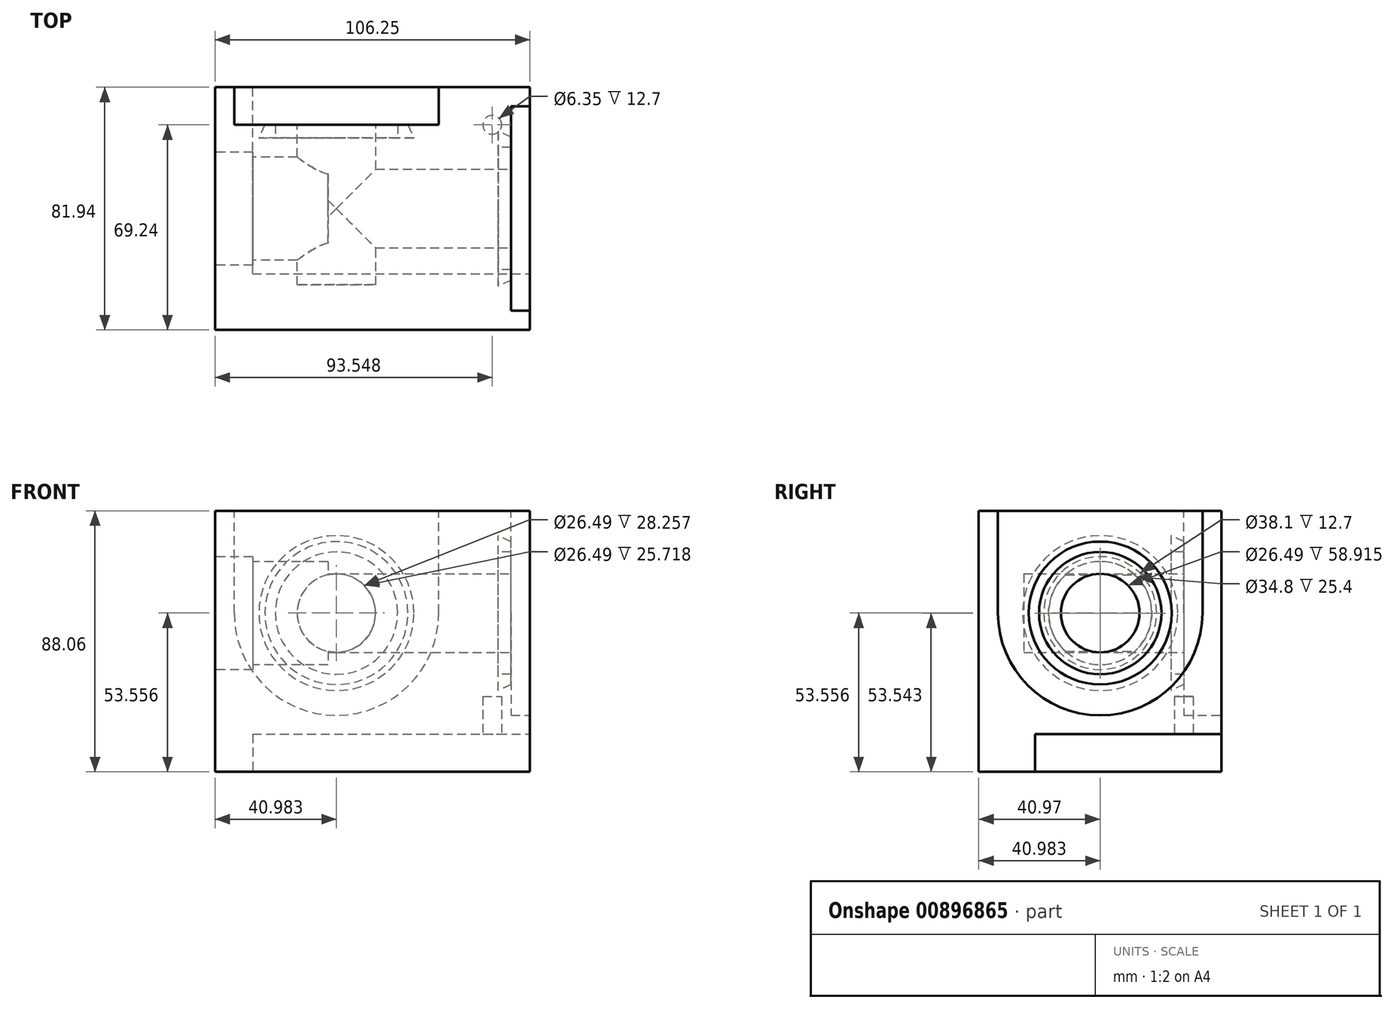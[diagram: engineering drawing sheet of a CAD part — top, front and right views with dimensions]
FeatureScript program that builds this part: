
annotation { "Feature Type Name" : "Feature", "Feature Type Description" : "" }
export const myFeature = defineFeature(function(context is Context, id is Id, definition is map)
    precondition{}
    {
        {
            var Q0;
            Q0=qCreatedBy(makeId("Top.planeOp"),FACE);
            var sketch = newSketch(context, id + "F0", { "sketchPlane" : qUnion([Q0])});
            skLineSegment(sketch, "E0.bottom", {"start": v(0, 0) * mm, "end": v(106.25, 0) * mm});
            skLineSegment(sketch, "E0.top", {"start": v(0, 81.94) * mm, "end": v(106.25, 81.94) * mm});
            skLineSegment(sketch, "E0.left", {"start": v(0, 0) * mm, "end": v(0, 81.94) * mm});
            skLineSegment(sketch, "E0.right", {"start": v(106.25, 0) * mm, "end": v(106.25, 81.94) * mm});
            skSolve(sketch);
        }
        {
            var Q0;
            Q0 = qSketchRegion(id + "F0", true);
            extrude(context, id + "F1", {"entities" : qUnion([Q0]), "depth" : 88.06 * mm, "offsetDistance" : 25.4 * mm});
        }
        {
            var Q0;
            Q0=makeQuery(id+"F1.opExtrude","SWEPT_FACE",FACE,{"disambiguationData":[OSD([sQuery(id+"F0.wireOp",EDGE,"E0.right")])]});
            var sketch = newSketch(context, id + "F2", { "sketchPlane" : qUnion([Q0])});
            skLineSegment(sketch, "E1.bottom", {"start": v(19.02, 0) * mm, "end": v(81.94, 0) * mm});
            skLineSegment(sketch, "E1.top", {"start": v(19.02, 12.7) * mm, "end": v(81.94, 12.7) * mm});
            skLineSegment(sketch, "E1.left", {"start": v(19.02, 0) * mm, "end": v(19.02, 12.7) * mm});
            skLineSegment(sketch, "E1.right", {"start": v(81.94, 0) * mm, "end": v(81.94, 12.7) * mm});
            skSolve(sketch);
        }
        {
            var Q0;
            Q0 = qSketchRegion(id + "F2", true);
            extrude(context, id + "F3", {"entities" : qUnion([Q0]), "operationType" : NewBodyOperationType.REMOVE, "oppositeDirection" : true, "depth" : 93.55 * mm, "offsetDistance" : 25.4 * mm});
        }
        {
            var Q0;
            Q0=makeQuery(id+"F1.opExtrude","SWEPT_FACE",FACE,{"disambiguationData":[OSD([sQuery(id+"F0.wireOp",EDGE,"E0.right")])]});
            var sketch = newSketch(context, id + "F4", { "sketchPlane" : qUnion([Q0])});
            skLineSegment(sketch, "E2.bottom", {"start": v(6.48, 53.56) * mm, "end": v(75.49, 53.56) * mm});
            skLineSegment(sketch, "E2.top", {"start": v(6.48, 88.06) * mm, "end": v(75.49, 88.06) * mm});
            skLineSegment(sketch, "E2.left", {"start": v(6.48, 53.56) * mm, "end": v(6.48, 88.06) * mm});
            skLineSegment(sketch, "E2.right", {"start": v(75.49, 53.56) * mm, "end": v(75.49, 88.06) * mm});
            skArc(sketch, "E3", {"start": v(75.49, 53.56) * mm, "mid": v(40.98, 19.05) * mm, "end": v(6.48, 53.56) * mm});
            skSolve(sketch);
        }
        {
            var Q0;
            Q0 = qSketchRegion(id + "F4", true);
            extrude(context, id + "F5", {"entities" : qUnion([Q0]), "operationType" : NewBodyOperationType.REMOVE, "oppositeDirection" : true, "depth" : 6.35 * mm, "offsetDistance" : 25.4 * mm});
        }
        {
            var Q0;
            Q0=makeQuery(id+"F1.opExtrude","SWEPT_FACE",FACE,{"disambiguationData":[OSD([sQuery(id+"F0.wireOp",EDGE,"E0.top")])]});
            var sketch = newSketch(context, id + "F6", { "sketchPlane" : qUnion([Q0])});
            skLineSegment(sketch, "E4.bottom", {"start": v(-75.49, 53.56) * mm, "end": v(-6.48, 53.56) * mm});
            skLineSegment(sketch, "E4.top", {"start": v(-75.49, 88.06) * mm, "end": v(-6.48, 88.06) * mm});
            skLineSegment(sketch, "E4.left", {"start": v(-75.49, 53.56) * mm, "end": v(-75.49, 88.06) * mm});
            skLineSegment(sketch, "E4.right", {"start": v(-6.48, 53.56) * mm, "end": v(-6.48, 88.06) * mm});
            skArc(sketch, "E5", {"start": v(-6.48, 53.56) * mm, "mid": v(-40.98, 19.05) * mm, "end": v(-75.49, 53.56) * mm});
            skSolve(sketch);
        }
        {
            var Q0;
            Q0 = qSketchRegion(id + "F6", true);
            extrude(context, id + "F7", {"entities" : qUnion([Q0]), "operationType" : NewBodyOperationType.REMOVE, "oppositeDirection" : true, "depth" : 12.7 * mm, "offsetDistance" : 25.4 * mm});
        }
        {
            var Q0;
            Q0=makeQuery(id+"F5.boolean.opBoolean","COPY",FACE,{"derivedFrom":makeQuery(id+"F5.opExtrude","CAP_FACE",FACE,{"disambiguationData":[OSD([sQuery(id+"F4.wireOp",EDGE,"E2.top"),sQuery(id+"F4.wireOp",EDGE,"E2.left"),sQuery(id+"F4.wireOp",EDGE,"E2.right"),sQuery(id+"F4.wireOp",EDGE,"E3")])],"isStart":false})});
            var sketch = newSketch(context, id + "F8", { "sketchPlane" : qUnion([Q0])});
            skCircle(sketch, "E6", {"center": v(40.98, 53.56) * mm, "radius": 13.25 * mm});
            skSolve(sketch);
        }
        {
            var Q0;
            Q0 = qSketchRegion(id + "F8", true);
            extrude(context, id + "F9", {"entities" : qUnion([Q0]), "operationType" : NewBodyOperationType.REMOVE, "oppositeDirection" : true, "depth" : 69.01 * mm, "offsetDistance" : 25.4 * mm});
        }
        {
            var Q0;
            Q0=makeQuery(id+"F7.boolean.opBoolean","COPY",FACE,{"derivedFrom":makeQuery(id+"F7.opExtrude","CAP_FACE",FACE,{"disambiguationData":[OSD([sQuery(id+"F6.wireOp",EDGE,"E4.top"),sQuery(id+"F6.wireOp",EDGE,"E4.left"),sQuery(id+"F6.wireOp",EDGE,"E4.right"),sQuery(id+"F6.wireOp",EDGE,"E5")])],"isStart":false})});
            var sketch = newSketch(context, id + "F10", { "sketchPlane" : qUnion([Q0])});
            skCircle(sketch, "E7", {"center": v(-40.98, 53.56) * mm, "radius": 13.25 * mm});
            skSolve(sketch);
        }
        {
            var Q0;
            Q0 = qSketchRegion(id + "F10", true);
            extrude(context, id + "F11", {"entities" : qUnion([Q0]), "operationType" : NewBodyOperationType.REMOVE, "oppositeDirection" : true, "depth" : 53.97 * mm, "offsetDistance" : 25.4 * mm});
        }
        {
            var Q0;
            Q0=makeQuery(id+"F1.opExtrude","SWEPT_FACE",FACE,{"disambiguationData":[OSD([sQuery(id+"F0.wireOp",EDGE,"E0.left")])]});
            var sketch = newSketch(context, id + "F12", { "sketchPlane" : qUnion([Q0])});
            skCircle(sketch, "E8", {"center": v(-40.97, 53.54) * mm, "radius": 19.05 * mm});
            skSolve(sketch);
        }
        {
            var Q0;
            Q0 = qSketchRegion(id + "F12", true);
            extrude(context, id + "F13", {"entities" : qUnion([Q0]), "operationType" : NewBodyOperationType.REMOVE, "oppositeDirection" : true, "depth" : 12.7 * mm, "offsetDistance" : 25.4 * mm});
        }
        {
            var Q0;
            Q0=makeQuery(id+"F3.boolean.opBoolean","COPY",FACE,{"derivedFrom":makeQuery(id+"F3.opExtrude","SWEPT_FACE",FACE,{"disambiguationData":[OSD([sQuery(id+"F2.wireOp",EDGE,"E1.top")])]})});
            var sketch = newSketch(context, id + "F14", { "sketchPlane" : qUnion([Q0])});
            skCircle(sketch, "E9", {"center": v(93.55, -69.24) * mm, "radius": 3.18 * mm});
            skSolve(sketch);
        }
        {
            var Q0;
            Q0 = qSketchRegion(id + "F14", true);
            extrude(context, id + "F15", {"entities" : qUnion([Q0]), "operationType" : NewBodyOperationType.REMOVE, "oppositeDirection" : true, "depth" : 12.7 * mm, "offsetDistance" : 25.4 * mm});
        }
        {
            var Q0;
            Q0=makeQuery(id+"F5.boolean.opBoolean","COPY",FACE,{"derivedFrom":makeQuery(id+"F5.opExtrude","CAP_FACE",FACE,{"disambiguationData":[OSD([sQuery(id+"F4.wireOp",EDGE,"E2.top"),sQuery(id+"F4.wireOp",EDGE,"E2.left"),sQuery(id+"F4.wireOp",EDGE,"E2.right"),sQuery(id+"F4.wireOp",EDGE,"E3")])],"isStart":false})});
            var sketch = newSketch(context, id + "F16", { "sketchPlane" : qUnion([Q0])});
            skCircle(sketch, "E10", {"center": v(40.98, 53.56) * mm, "radius": 24.12 * mm});
            skSolve(sketch);
        }
        {
            var Q0;
            Q0 = qSketchRegion(id + "F16", true);
            extrude(context, id + "F17", {"entities" : qUnion([Q0]), "operationType" : NewBodyOperationType.REMOVE, "oppositeDirection" : true, "depth" : 4.37 * mm, "offsetDistance" : 25.4 * mm, "hasDraft" : true, "draftAngle" : 25 * degree});
        }
        {
            var Q0;
            Q0=makeQuery(id+"F17.boolean.opBoolean","COPY",FACE,{"derivedFrom":makeQuery(id+"F17.opExtrude","CAP_FACE",FACE,{"disambiguationData":[OSD([sQuery(id+"F16.wireOp",EDGE,"E10")])],"isStart":false})});
            var sketch = newSketch(context, id + "F18", { "sketchPlane" : qUnion([Q0])});
            skCircle(sketch, "E11", {"center": v(40.98, 53.56) * mm, "radius": 20.64 * mm});
            skSolve(sketch);
        }
        {
            var Q0;
            Q0 = qSketchRegion(id + "F18", true);
            extrude(context, id + "F19", {"entities" : qUnion([Q0]), "operationType" : NewBodyOperationType.ADD, "depth" : 4.37 * mm, "offsetDistance" : 25.4 * mm});
        }
        {
            var Q0;
            Q0=makeQuery(id+"F19.opExtrude","CAP_FACE",FACE,{"disambiguationData":[OSD([sQuery(id+"F18.wireOp",EDGE,"E11")])],"isStart":false});
            var sketch = newSketch(context, id + "F20", { "sketchPlane" : qUnion([Q0])});
            skCircle(sketch, "E12", {"center": v(40.98, 53.56) * mm, "radius": 13.25 * mm});
            skSolve(sketch);
        }
        {
            var Q0;
            Q0 = qSketchRegion(id + "F20", true);
            extrude(context, id + "F21", {"entities" : qUnion([Q0]), "operationType" : NewBodyOperationType.REMOVE, "oppositeDirection" : true, "depth" : 25.4 * mm, "offsetDistance" : 25.4 * mm});
        }
        {
            var Q0;
            Q0=makeQuery(id+"F7.boolean.opBoolean","COPY",FACE,{"derivedFrom":makeQuery(id+"F7.opExtrude","CAP_FACE",FACE,{"disambiguationData":[OSD([sQuery(id+"F6.wireOp",EDGE,"E4.top"),sQuery(id+"F6.wireOp",EDGE,"E4.left"),sQuery(id+"F6.wireOp",EDGE,"E4.right"),sQuery(id+"F6.wireOp",EDGE,"E5")])],"isStart":false})});
            var sketch = newSketch(context, id + "F22", { "sketchPlane" : qUnion([Q0])});
            skCircle(sketch, "E13", {"center": v(-40.98, 53.56) * mm, "radius": 24.12 * mm});
            skSolve(sketch);
        }
        {
            var Q0;
            Q0=makeQuery(id+"F13.boolean.opBoolean","COPY",FACE,{"derivedFrom":makeQuery(id+"F13.opExtrude","CAP_FACE",FACE,{"disambiguationData":[OSD([sQuery(id+"F12.wireOp",EDGE,"E8")])],"isStart":false})});
            var sketch = newSketch(context, id + "F23", { "sketchPlane" : qUnion([Q0])});
            skCircle(sketch, "E14", {"center": v(-40.97, 53.54) * mm, "radius": 17.4 * mm});
            skSolve(sketch);
        }
        {
            var Q0;
            Q0 = qSketchRegion(id + "F23", true);
            extrude(context, id + "F24", {"entities" : qUnion([Q0]), "operationType" : NewBodyOperationType.REMOVE, "oppositeDirection" : true, "depth" : 25.4 * mm, "offsetDistance" : 25.4 * mm});
        }
        {
            var Q0;
            Q0=makeQuery(id+"F22.imprint","IMPRINT",FACE,{"disambiguationData":[TD([[makeQuery(id+"F22.imprint","IMPRINT",EDGE,{"derivedFrom":sQuery(id+"F22.wireOp",EDGE,"E13")}),1.0]])]});
            var Q1;
            Q1 = qSketchRegion(id + "F22", true);
            extrude(context, id + "F25", {"entities" : qUnion([Q0, Q1]), "operationType" : NewBodyOperationType.REMOVE, "oppositeDirection" : true, "depth" : 4.37 * mm, "offsetDistance" : 25.4 * mm, "hasDraft" : true, "draftAngle" : 25 * degree});
        }
        {
            var Q0;
            Q0=makeQuery(id+"F25.boolean.opBoolean","COPY",FACE,{"derivedFrom":makeQuery(id+"F25.opExtrude","CAP_FACE",FACE,{"disambiguationData":[OSD([sQuery(id+"F22.wireOp",EDGE,"E13")])],"isStart":false})});
            var sketch = newSketch(context, id + "F26", { "sketchPlane" : qUnion([Q0])});
            skCircle(sketch, "E15", {"center": v(-40.98, 53.56) * mm, "radius": 20.64 * mm});
            skSolve(sketch);
        }
        {
            var Q0;
            Q0 = qSketchRegion(id + "F26", true);
            extrude(context, id + "F27", {"entities" : qUnion([Q0]), "operationType" : NewBodyOperationType.ADD, "depth" : 4.37 * mm, "offsetDistance" : 25.4 * mm});
        }
        {
            var Q0;
            Q0=makeQuery(id+"F27.opExtrude","CAP_FACE",FACE,{"disambiguationData":[OSD([sQuery(id+"F26.wireOp",EDGE,"E15")])],"isStart":false});
            var sketch = newSketch(context, id + "F28", { "sketchPlane" : qUnion([Q0])});
            skCircle(sketch, "E16", {"center": v(-40.98, 53.56) * mm, "radius": 13.25 * mm});
            skSolve(sketch);
        }
        {
            var Q0;
            Q0 = qSketchRegion(id + "F28", true);
            extrude(context, id + "F29", {"entities" : qUnion([Q0]), "operationType" : NewBodyOperationType.REMOVE, "endBound" : BoundingType.UP_TO_NEXT, "oppositeDirection" : true, "depth" : 25.4 * mm, "offsetDistance" : 25.4 * mm});
        }
    });
